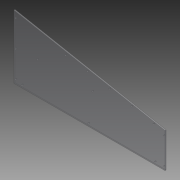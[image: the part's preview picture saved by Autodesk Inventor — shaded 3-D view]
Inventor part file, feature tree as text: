
AUTODESK INVENTOR PART (.ipt)
format: ipt  version: 2014 SP1 (Build 180222100, 222)  size: 107,520 bytes
history: native  units: in
note: dims shown in document units (in); Inventor stores cm internally (conversion verified against a paired STEP export)
features: reference x7, extrude x1, sketch x1
ambient origin geometry x8: Origin, YZ Plane, XZ Plane, XY Plane, X Axis, Y Axis, Z Axis, Center Point
bodies: Solid1 (feature_tree)
feature tree (9):
  extrude  "Extrusion1"  Depth=0.125in TaperAngle=0.0deg
  sketch  "Sketch1"  dims[d3=18.75in d6=0.125in d7=0.0in d8=4.2478in d9=7.75in d10=18.4438in]
  reference  "Reference1"
  reference  "Reference2"
  reference  "Reference3"
  reference  "Reference4"
  reference  "Reference5"
  reference  "Reference6"
  reference  "Reference7"
